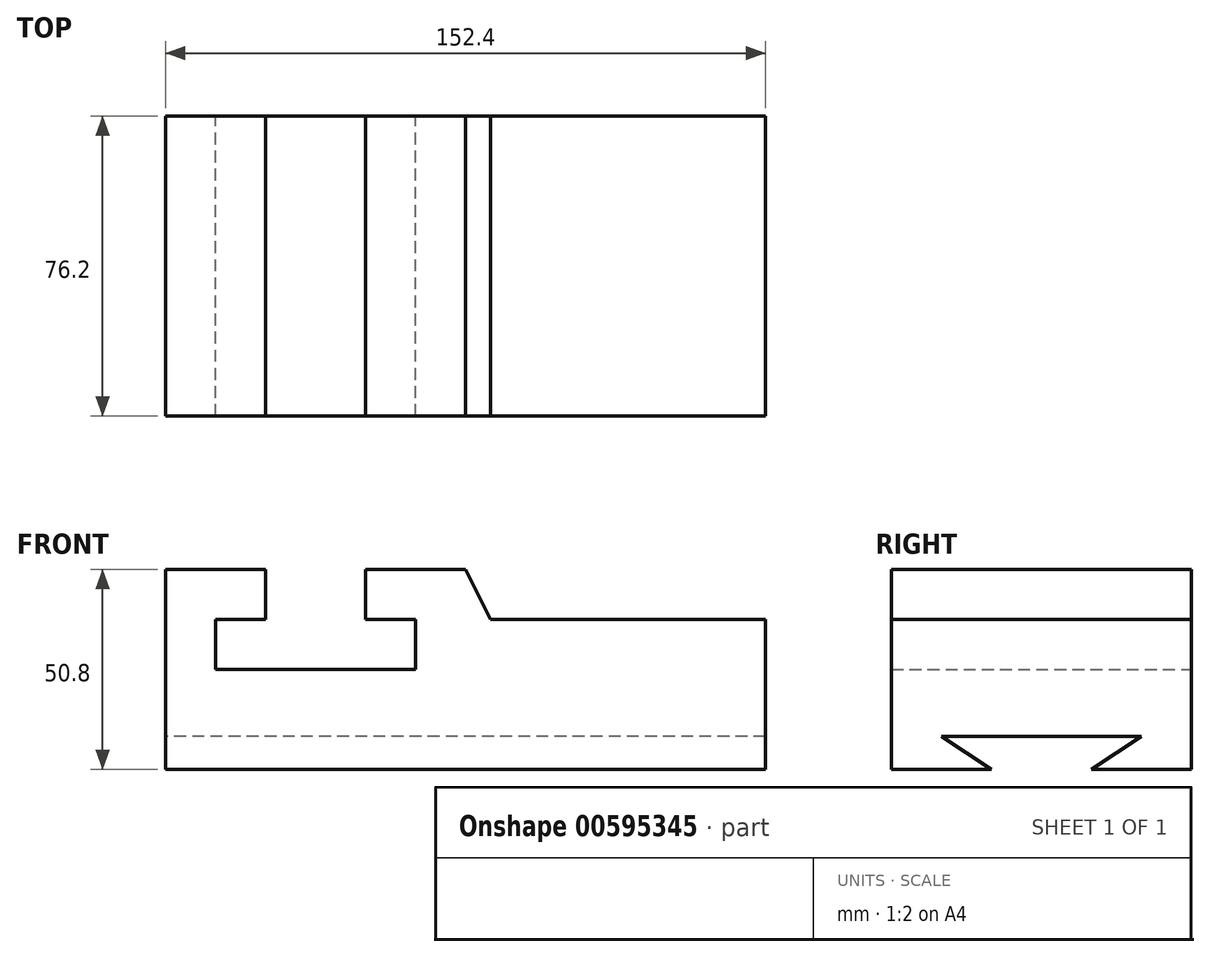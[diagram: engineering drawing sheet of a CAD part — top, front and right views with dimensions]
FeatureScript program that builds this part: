
annotation { "Feature Type Name" : "Feature", "Feature Type Description" : "" }
export const myFeature = defineFeature(function(context is Context, id is Id, definition is map)
    precondition{}
    {
        {
            var Q0;
            Q0=qCreatedBy(makeId("Front.planeOp"),FACE);
            var sketch = newSketch(context, id + "F0", { "sketchPlane" : qUnion([Q0])});
            skLineSegment(sketch, "E0.bottom", {"start": v(0, 0) * mm, "end": v(152.4, 0) * mm});
            skLineSegment(sketch, "E0.top", {"start": v(0, 50.8) * mm, "end": v(25.4, 50.8) * mm});
            skLineSegment(sketch, "E0.left", {"start": v(0, 0) * mm, "end": v(0, 50.8) * mm});
            skLineSegment(sketch, "E0.right", {"start": v(152.4, 0) * mm, "end": v(152.4, 38.1) * mm});
            skLineSegment(sketch, "E1", {"start": v(25.4, 50.8) * mm, "end": v(25.4, 38.1) * mm});
            skLineSegment(sketch, "E2", {"start": v(25.4, 38.1) * mm, "end": v(12.7, 38.1) * mm});
            skLineSegment(sketch, "E3", {"start": v(12.7, 38.1) * mm, "end": v(12.7, 25.4) * mm});
            skLineSegment(sketch, "E4", {"start": v(12.7, 25.4) * mm, "end": v(63.5, 25.4) * mm});
            skLineSegment(sketch, "E5", {"start": v(63.5, 25.4) * mm, "end": v(63.5, 38.1) * mm});
            skLineSegment(sketch, "E6", {"start": v(63.5, 38.1) * mm, "end": v(50.8, 38.1) * mm});
            skLineSegment(sketch, "E7", {"start": v(50.8, 38.1) * mm, "end": v(50.8, 50.8) * mm});
            skLineSegment(sketch, "E8", {"start": v(82.55, 38.1) * mm, "end": v(152.4, 38.1) * mm});
            skLineSegment(sketch, "E9", {"start": v(76.2, 50.8) * mm, "end": v(82.55, 38.1) * mm});
            skLineSegment(sketch, "E10", {"start": v(82.55, 38.1) * mm, "end": v(82.55, 38.1) * mm});
            skPoint(sketch, "E11.orphan", {"position": v(76.2, 38.1) * mm});
            skPoint(sketch, "E12.orphan", {"position": v(152.4, 50.8) * mm});
            skLineSegment(sketch, "E13.trimOffspring", {"start": v(50.8, 50.8) * mm, "end": v(76.2, 50.8) * mm});
            skSolve(sketch);
        }
        {
            var Q0;
            Q0 = qSketchRegion(id + "F0", true);
            extrude(context, id + "F1", {"entities" : qUnion([Q0]), "depth" : 76.2 * mm, "offsetDistance" : 25.4 * mm});
        }
        {
            var Q0;
            Q0=makeQuery(id+"F1.opExtrude","SWEPT_FACE",FACE,{"disambiguationData":[OSD([sQuery(id+"F0.wireOp",EDGE,"E0.left")])]});
            cPlane(context, id + "F2", {"entities" : qUnion([Q0]), "cplaneType" : CPlaneType.OFFSET, "offset" : 25.4 * mm, "width" : 152.4 * mm, "height" : 152.4 * mm});
        }
        {
            var Q0;
            Q0=qCreatedBy(id+"F2.planeOp",FACE);
            var sketch = newSketch(context, id + "F3", { "sketchPlane" : qUnion([Q0])});
            skLineSegment(sketch, "E14", {"start": v(12.7, 8.43) * mm, "end": v(63.5, 8.43) * mm});
            skLineSegment(sketch, "E15", {"start": v(12.7, 8.43) * mm, "end": v(25.4, 0) * mm});
            skLineSegment(sketch, "E16", {"start": v(63.5, 8.43) * mm, "end": v(50.8, 0) * mm});
            skPoint(sketch, "E17.start.orphan", {"position": v(12.7, 0) * mm});
            skLineSegment(sketch, "E18.trimOffspring", {"start": v(25.4, 0) * mm, "end": v(50.8, 0) * mm});
            skPoint(sketch, "E19.trimOffspring.start.orphan", {"position": v(63.5, 0) * mm});
            skSolve(sketch);
        }
        {
            var Q0;
            Q0 = qSketchRegion(id + "F3", true);
            extrude(context, id + "F4", {"entities" : qUnion([Q0]), "operationType" : NewBodyOperationType.REMOVE, "oppositeDirection" : true, "depth" : 187.96 * mm, "offsetDistance" : 25.4 * mm});
        }
    });
